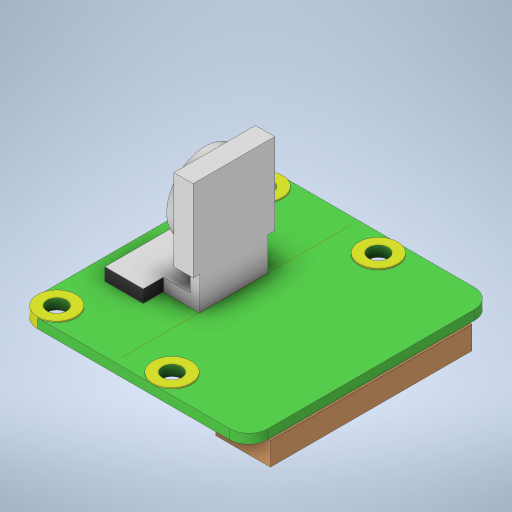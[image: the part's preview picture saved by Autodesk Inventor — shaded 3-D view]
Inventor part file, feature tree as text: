
AUTODESK INVENTOR PART (.ipt)
format: ipt  version: 2023 (Build 270158000, 158)  size: 374,272 bytes
history: native  units: mm
features: extrude x9, sketch x7, other x2, fillet x1, mirror x1, pattern_linear x1
ambient origin geometry x8: Origin, YZ Plane, XZ Plane, XY Plane, X Axis, Y Axis, Z Axis, Center Point
bodies: Body1 (feature_tree)
feature tree (21):
  other  "솔리드1"
  sketch  "스케치1"
  extrude  "돌출1"  Depth=25.5mm
  extrude  "돌출2"  Depth=24.0mm
  extrude  "돌출3"  Depth=8.5mm
  fillet  "모깎기1"  Radius=8.5mm
  mirror  "미러3"
  pattern_linear  "직사각형 패턴1"  Spacing1=17.7mm  [1 undecoded]
  sketch  "스케치2"
  extrude  "돌출7"  Depth=1.0mm
  extrude  "돌출8"  Depth=7.1mm
  extrude  "돌출9"  Depth=4.0mm
  other  "작업 평면1"
  sketch  "스케치7"
  extrude  "돌출10"  Depth=7.0mm
  extrude  "돌출11"  Depth=9.2mm
  extrude  "돌출12"  Depth=2.0mm
  sketch  "스케치4"
  sketch  "스케치5"
  sketch  "스케치6"
  sketch  "스케치8"
note: 1 required parameter value undecoded (feature->parameter linkage not recoverable at this tier; creation-order binding heuristic only, values carry confidence <= 0.55)
